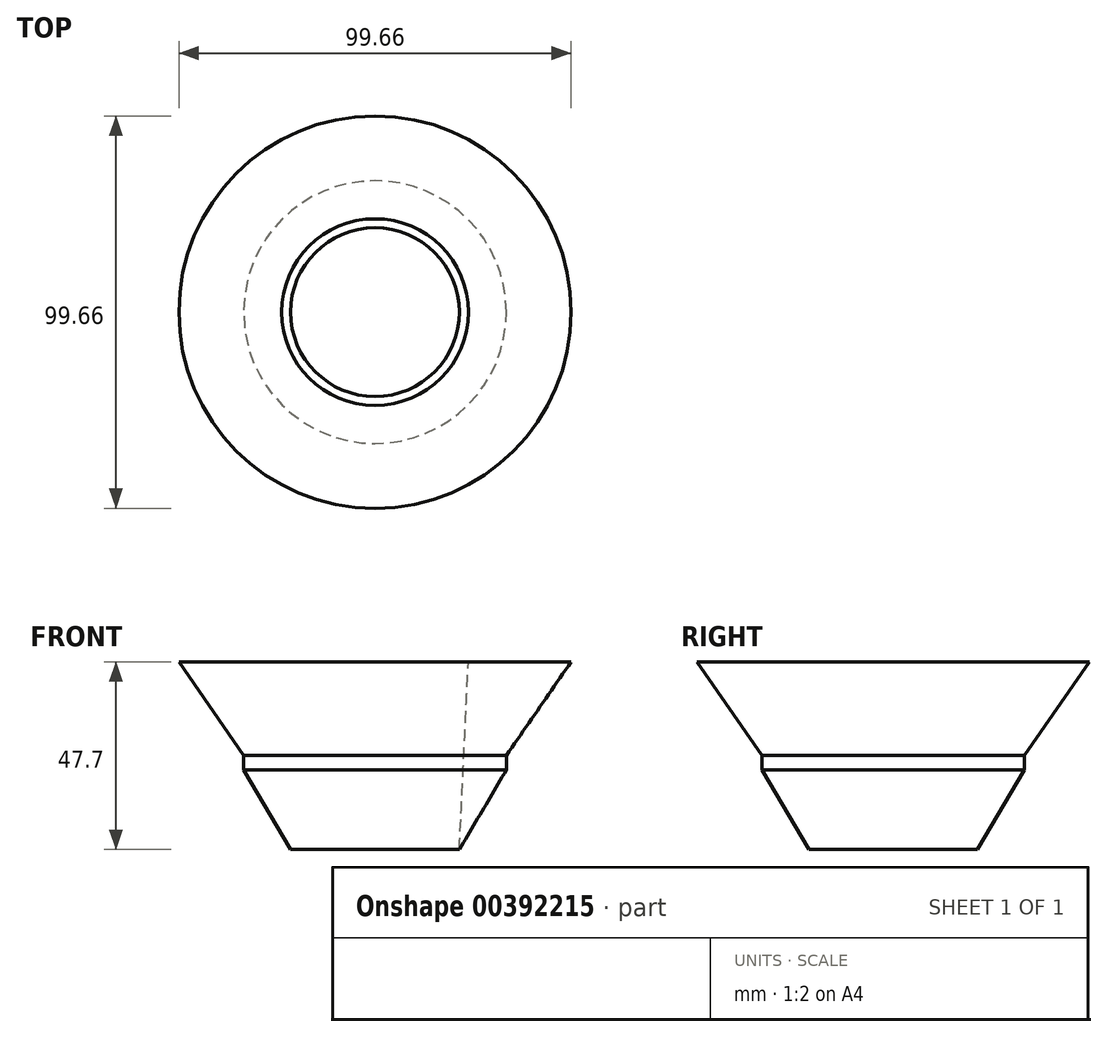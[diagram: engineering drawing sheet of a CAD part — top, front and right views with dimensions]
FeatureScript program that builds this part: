
annotation { "Feature Type Name" : "Feature", "Feature Type Description" : "" }
export const myFeature = defineFeature(function(context is Context, id is Id, definition is map)
    precondition{}
    {
        {
            var Q0;
            Q0=qCreatedBy(makeId("Front.planeOp"),FACE);
            var sketch = newSketch(context, id + "F0", { "sketchPlane" : qUnion([Q0])});
            skLineSegment(sketch, "E0", {"start": v(-21.44, -20.16) * mm, "end": v(-33.36, 0) * mm});
            skLineSegment(sketch, "E1", {"start": v(-33.36, 0) * mm, "end": v(-33.36, 3.7) * mm});
            skLineSegment(sketch, "E2", {"start": v(-33.36, 3.7) * mm, "end": v(-49.83, 27.54) * mm});
            skLineSegment(sketch, "E3", {"start": v(-49.83, 27.54) * mm, "end": v(-23.7, 27.54) * mm});
            skLineSegment(sketch, "E4", {"start": v(-23.7, 27.54) * mm, "end": v(-21.44, -20.16) * mm});
            skLineSegment(sketch, "E5", {"start": v(0, 26.45) * mm, "end": v(0, -17.44) * mm});
            skSolve(sketch);
        }
        {
            var Q0;
            Q0 = qSketchRegion(id + "F0", true);
            var Q1;
            Q1=sQuery(id+"F0.wireOp",EDGE,"E5");
            revolve(context, id + "F1", {"entities" : qUnion([Q0]), "axis" : qUnion([Q1]), "revolveType" : RevolveType.FULL});
        }
    });
